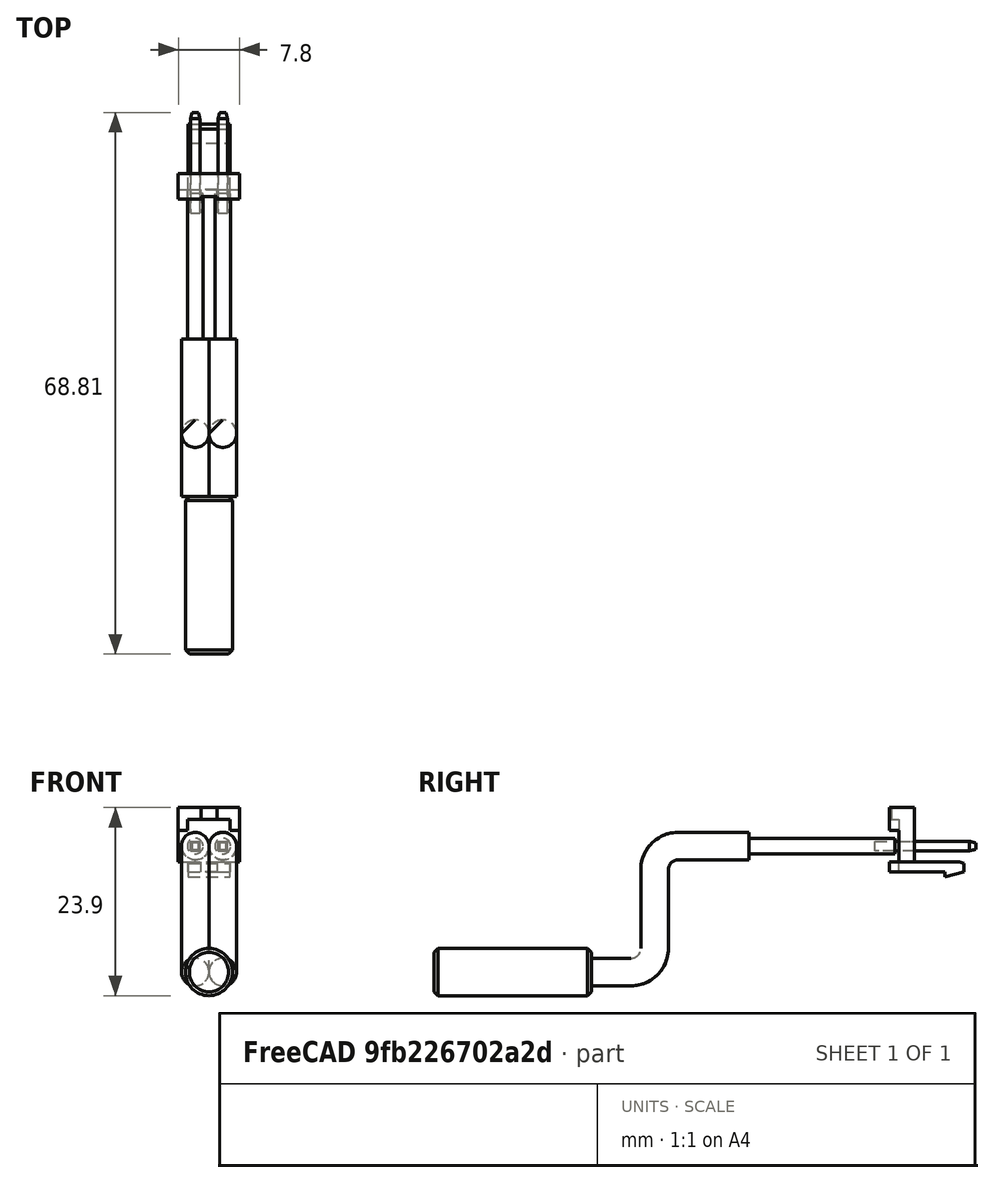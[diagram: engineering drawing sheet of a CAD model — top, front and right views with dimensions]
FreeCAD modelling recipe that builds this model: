
FCSTD DOCUMENT  (FreeCAD 0.14R3702 (Git))
Label: hotend-heater-cartridge
License: CC-BY 3.0
LicenseURL: http://creativecommons.org/licenses/by/3.0/
objects: Part::Feature×5, Part::Cylinder×2, Part::MultiFuse×2, Part::Compound×2, Part::Chamfer×1, Part::Plane×1, Part::Part2DObjectPython×1, Part::Sweep×1, App::DocumentObjectGroup×1
note: 15 computed .brp shape members not serialized (recipe doc carries the construction recipe); baked Part::Feature solids carry a one-line shape summary decoded from their .brp

FEATURE [Part::Cylinder] Cylinder  label="cartridge-main-body-sketch"
  Angle = 360
  Height = 20
  Placement = pos=(-0.00335414,-17.0135,0.000689865) rot=(1,0,0;1.5708rad)
  Radius = 3
FEATURE [Part::Chamfer] Chamfer  label="cartridge-main-body"
  Base = -> Cylinder
  Edges = 2 edges r=0.5: [Edge1,Edge3]
FEATURE [Part::Plane] Plane
  Length = 10
  Placement = pos=(1.74665,-17.0135,0.000689865) rot=(0,1,0;1.5708rad)
  Width = 10
FEATURE [Part::Feature] Wire  label="Wire-path"
  shape: bbox 2e-07 x 20 x 16 mm, 0 faces, 0 solids (baked)
FEATURE [Part::Part2DObjectPython] Circle  label="wire-section"  # Draft 2D object (typed FeaturePython)
  FirstAngle = 0
  LastAngle = 0
  MakeFace = false
  Placement = pos=(1.74665,-17.0135,0.000689865) rot=(-1,0,0;1.5708rad)
  Radius = 1.75
  Support = -> Chamfer
FEATURE [Part::Sweep] Sweep  label="wire-1-section-1"
  Frenet = true
  Sections = -> [Circle]
  Solid = true
  Spine = -> Wire [Edge1,Edge2,Edge3,Edge4,Edge5]
  Transition = 1
FEATURE [Part::Cylinder] Cylinder001  label="wire-1-section-2"
  Angle = 360
  Height = 18.5
  Placement = pos=(1.74665,2.98645,16.0007) rot=(-1,0,0;1.5708rad)
  Radius = 1
FEATURE [Part::MultiFuse] Fusion  label="wire-src"
  Shapes = -> [Sweep,Cylinder001]
FEATURE [Part::Feature] Fusion001  label="wire-2"
  Placement = pos=(-3.5,-4e-11,5e-12) rot=(0,0,1;0rad)
  shape: bbox 3.5 x 38.5 x 20.28 mm, 9 faces (baked)
FEATURE [Part::Feature] Fusion002  label="wire-1"
  shape: bbox 3.5 x 38.5 x 20.28 mm, 9 faces (baked)
FEATURE [Part::MultiFuse] Fusion003  label="wires"
  Shapes = -> [Fusion001,Fusion002]
FEATURE [App::DocumentObjectGroup] Group  label="src"
  Group = -> [Chamfer,Plane,Wire,Fusion,Fusion003]
FEATURE [Part::Feature] Chamfer001  label="cartridge-main-body-final"
  shape: bbox 6 x 20 x 6 mm, 5 faces (baked)
FEATURE [Part::Feature] Fusion003001  label="cardtridge-wires-final"
  shape: bbox 7 x 38.5 x 20.28 mm, 23 faces, 2 solids (baked)
FEATURE [Part::Compound] Compound002  label="heater-cartridge-connector-final"
  Placement = pos=(-0.00335419,24,14.0007) rot=(0,0,1;1.5708rad)
FEATURE [Part::Compound] Compound003  label="hotend-heater-cartridge"
  Links = -> [Chamfer001,Fusion003001,Compound002]
